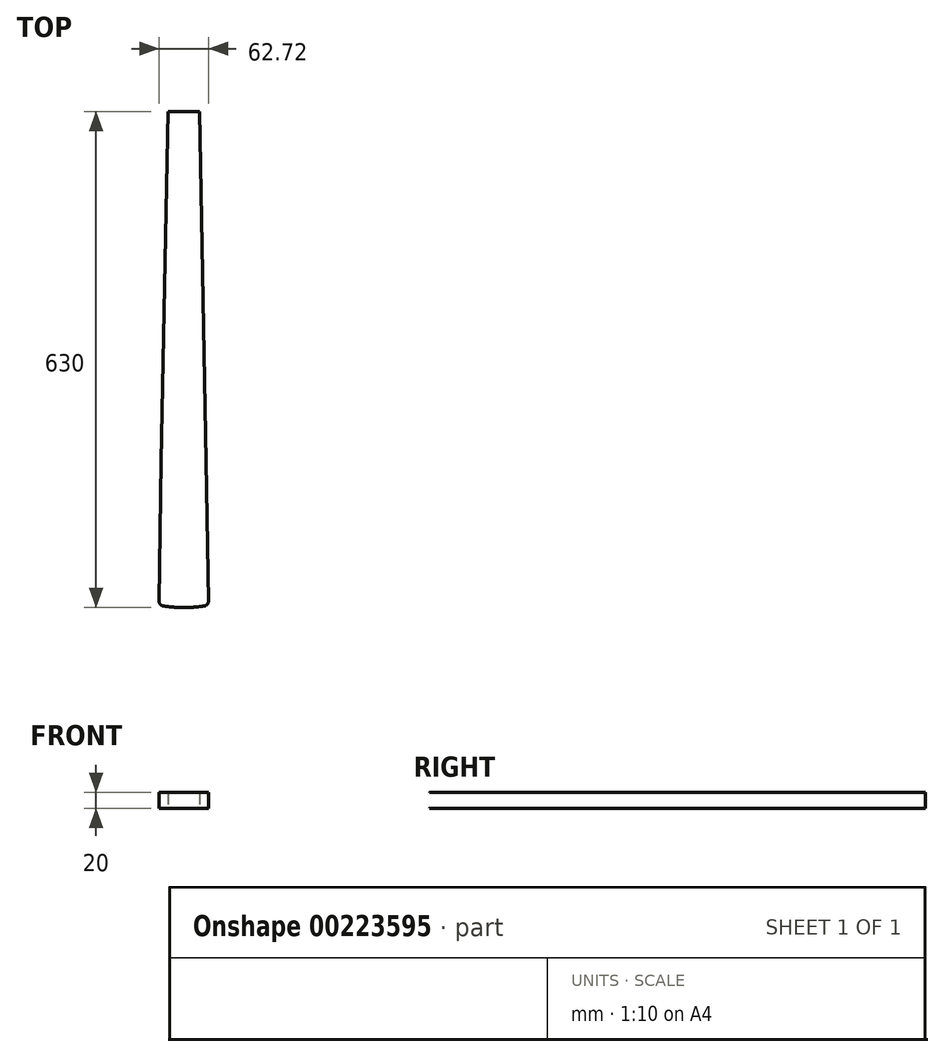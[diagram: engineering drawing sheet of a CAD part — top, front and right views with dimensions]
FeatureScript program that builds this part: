
annotation { "Feature Type Name" : "Feature", "Feature Type Description" : "" }
export const myFeature = defineFeature(function(context is Context, id is Id, definition is map)
    precondition{}
    {
        {
            var Q0;
            Q0=qCreatedBy(makeId("Top.planeOp"),FACE);
            var sketch = newSketch(context, id + "F0", { "sketchPlane" : qUnion([Q0])});
            skLineSegment(sketch, "E0.0", {"start": v(-8.54, 158.09) * mm, "end": v(-11.36, -19.86) * mm});
            skArc(sketch, "E1.0", {"start": v(-6.36, -25.78) * mm, "mid": v(-9.97, -23.76) * mm, "end": v(-11.36, -19.86) * mm});
            skArc(sketch, "E2.0", {"start": v(20, -27.88) * mm, "mid": v(6.78, -27.35) * mm, "end": v(-6.36, -25.78) * mm});
            skLineSegment(sketch, "E3", {"start": v(20, -27.88) * mm, "end": v(20.02, 222.24) * mm, "construction": true});
            skLineSegment(sketch, "E4", {"start": v(20, -27.88) * mm, "end": v(77.58, -27.89) * mm, "construction": true});
            skLineSegment(sketch, "E5.direction1", {"start": v(20, -27.88) * mm, "end": v(69.08, -27.88) * mm, "construction": true});
            skLineSegment(sketch, "E5.direction2", {"start": v(20, -27.88) * mm, "end": v(20, 602.12) * mm, "construction": true});
            skLineSegment(sketch, "E6", {"start": v(20, 602.12) * mm, "end": v(0, 602.12) * mm});
            skLineSegment(sketch, "E7", {"start": v(0, 602.12) * mm, "end": v(-8.54, 158.09) * mm});
            skLineSegment(sketch, "E8.MirrorCS", {"start": v(48.54, 158.09) * mm, "end": v(51.36, -19.86) * mm});
            skArc(sketch, "E9.MirrorCS", {"start": v(46.36, -25.78) * mm, "mid": v(49.97, -23.76) * mm, "end": v(51.36, -19.86) * mm});
            skArc(sketch, "E10.MirrorCS", {"start": v(20, -27.88) * mm, "mid": v(33.22, -27.35) * mm, "end": v(46.36, -25.78) * mm});
            skLineSegment(sketch, "E11.MirrorCS", {"start": v(40, 602.12) * mm, "end": v(48.54, 158.09) * mm});
            skLineSegment(sketch, "E12", {"start": v(20, 602.12) * mm, "end": v(40, 602.12) * mm});
            skSolve(sketch);
        }
        {
            var Q0;
            Q0 = qSketchRegion(id + "F0", true);
            extrude(context, id + "F1", {"entities" : qUnion([Q0]), "depth" : 20 * mm});
        }
    });
